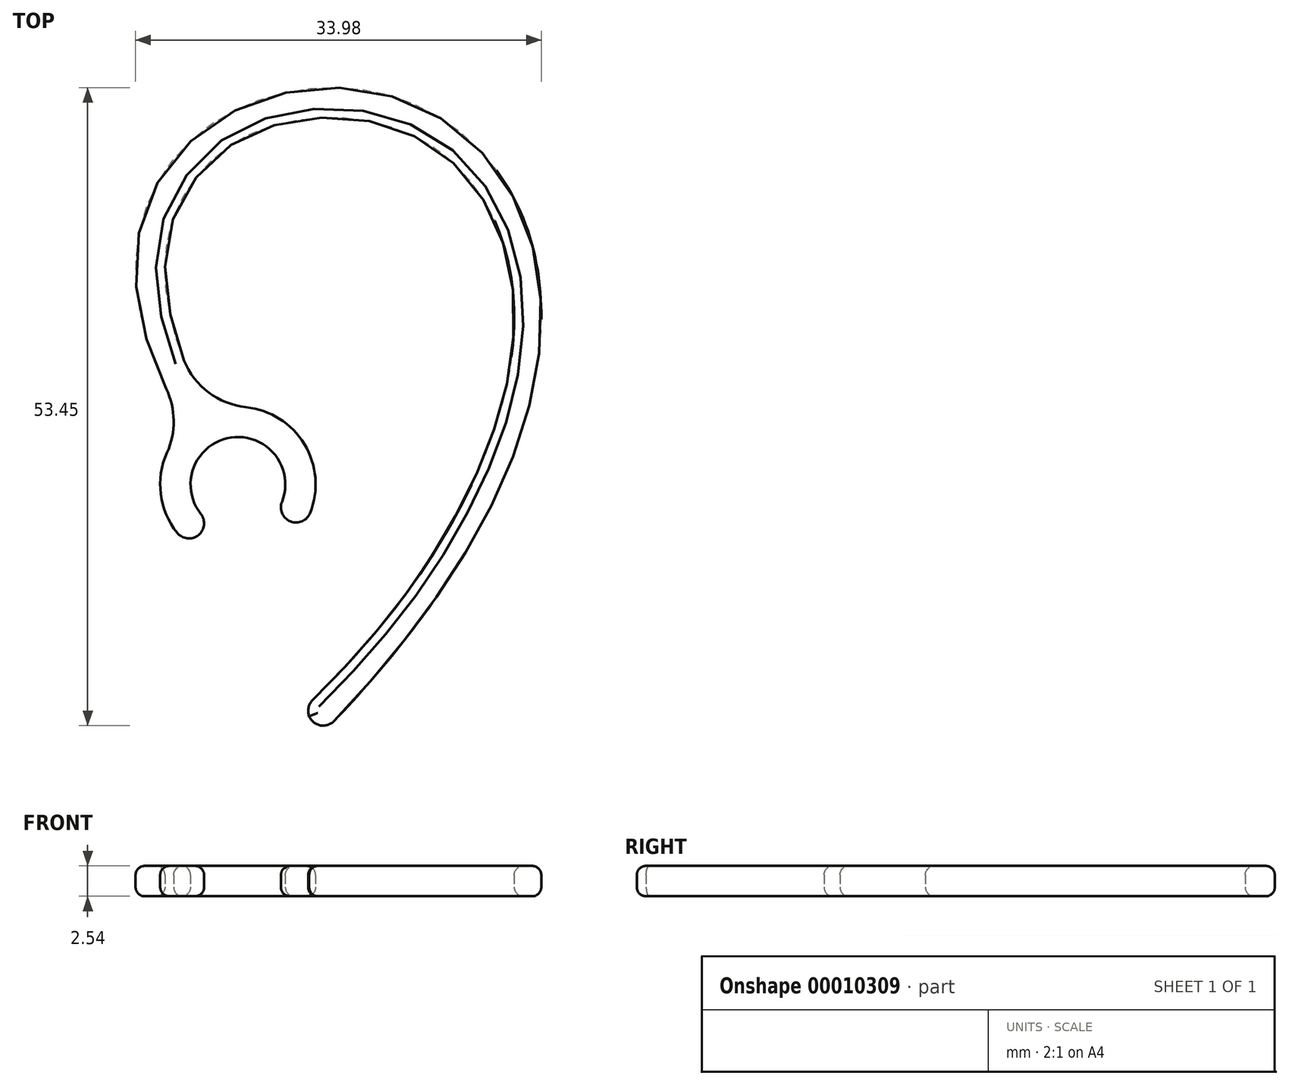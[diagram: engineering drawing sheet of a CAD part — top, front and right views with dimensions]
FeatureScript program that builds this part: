
annotation { "Feature Type Name" : "Feature", "Feature Type Description" : "" }
export const myFeature = defineFeature(function(context is Context, id is Id, definition is map)
    precondition{}
    {
        {
            var Q0;
            Q0=qCreatedBy(makeId("Top.planeOp"),FACE);
            var sketch = newSketch(context, id + "F0", { "sketchPlane" : qUnion([Q0])});
            skArc(sketch, "E0", {"start": v(3.23, -2.3) * mm, "mid": v(-0.58, 3.93) * mm, "end": v(-2.42, -3.15) * mm});
            skArc(sketch, "E1.0", {"start": v(5.3, -3.78) * mm, "mid": v(-0.96, 6.44) * mm, "end": v(-3.97, -5.16) * mm});
            skLineSegment(sketch, "E2", {"start": v(-2.42, -3.15) * mm, "end": v(-3.97, -5.16) * mm});
            skLineSegment(sketch, "E3", {"start": v(3.23, -2.3) * mm, "end": v(5.3, -3.78) * mm});
            skSolve(sketch);
        }
        {
            var Q0;
            Q0 = qSketchRegion(id + "F0", true);
            extrude(context, id + "F1", {"entities" : qUnion([Q0]), "depth" : 2.54 * mm});
        }
        {
            var Q0;
            Q0=qCreatedBy(makeId("Top.planeOp"),FACE);
            var sketch = newSketch(context, id + "F2", { "sketchPlane" : qUnion([Q0])});
            skFitSpline(sketch, "E4", {"points": [v(-2.9, 2.7) * mm, v(9.7, 33.15) * mm, v(6.7, -21.22) * mm], "startDerivative": vector(-95, 139.03) * mm, "endDerivative": vector(-160.2, -162.17) * mm});
            skFitSpline(sketch, "E5.0", {"points": [v(-0.8, 4.14) * mm, v(-2.68, 6.88) * mm, v(-4.63, 10.68) * mm, v(-5.82, 15.02) * mm, v(-6.11, 17.91) * mm, v(-5.9, 20.46) * mm, v(-5.25, 22.7) * mm, v(-4.23, 24.65) * mm, v(-2.43, 26.92) * mm, v(0.56, 29.13) * mm, v(4.2, 30.38) * mm, v(7.22, 30.74) * mm, v(9.46, 30.68) * mm, v(11.62, 30.3) * mm, v(14.38, 29.35) * mm, v(17.5, 27.42) * mm, v(20.48, 23.96) * mm, v(22.46, 19.4) * mm, v(23.14, 13.7) * mm, v(22.15, 6.89) * mm, v(19.11, -0.97) * mm, v(13.64, -9.75) * mm, v(8.15, -16.14) * mm, v(4.88, -19.44) * mm]});
            skLineSegment(sketch, "E6", {"start": v(5.66, -18.65) * mm, "end": v(6.7, -21.22) * mm});
            skArc(sketch, "E7.0", {"start": v(-0.97, 4.37) * mm, "mid": v(-2.17, 3.92) * mm, "end": v(-3.2, 3.14) * mm});
            skSolve(sketch);
        }
        {
            var Q0;
            Q0 = qSketchRegion(id + "F2", true);
            extrude(context, id + "F3", {"entities" : qUnion([Q0]), "operationType" : NewBodyOperationType.ADD, "depth" : 2.54 * mm});
        }
        {
            var Q0;
            Q0=makeQuery(id+"F3.boolean.opBoolean","INTERSECT",EDGE,{"derivedFrom":[makeQuery(id+"F1.opExtrude","SWEPT_FACE",FACE,{"disambiguationData":[OSD([sQuery(id+"F0.wireOp",EDGE,"E1.0")])]}),makeQuery(id+"F3.opExtrude","SWEPT_FACE",FACE,{"disambiguationData":[OSD([sQuery(id+"F2.wireOp",EDGE,"E4")])]})]});
            var Q1;
            Q1=makeQuery(id+"F3.boolean.opBoolean","INTERSECT",EDGE,{"derivedFrom":[makeQuery(id+"F1.opExtrude","SWEPT_FACE",FACE,{"disambiguationData":[OSD([sQuery(id+"F0.wireOp",EDGE,"E1.0")])]}),makeQuery(id+"F3.opExtrude","SWEPT_FACE",FACE,{"disambiguationData":[OSD([sQuery(id+"F2.wireOp",EDGE,"E5.0")])]})]});
            fillet(context, id + "F4", {"entities" : qUnion([Q0, Q1]), "radius" : 6.35 * mm, "tangentPropagation" : true, "allowEdgeOverflow" : false});
        }
        {
            var Q0;
            Q0=makeQuery(id+"F1.opExtrude","SWEPT_EDGE",EDGE,{"disambiguationData":[OSD([sQuery(id+"F0.wireOp",EDGE,"E0"),sQuery(id+"F0.wireOp",EDGE,"E3")])]});
            var Q1;
            Q1=makeQuery(id+"F1.opExtrude","SWEPT_EDGE",EDGE,{"disambiguationData":[OSD([sQuery(id+"F0.wireOp",EDGE,"E1.0"),sQuery(id+"F0.wireOp",EDGE,"E3")])]});
            var Q2;
            Q2=makeQuery(id+"F1.opExtrude","SWEPT_EDGE",EDGE,{"disambiguationData":[OSD([sQuery(id+"F0.wireOp",EDGE,"E1.0"),sQuery(id+"F0.wireOp",EDGE,"E2")])]});
            var Q3;
            Q3=makeQuery(id+"F1.opExtrude","SWEPT_EDGE",EDGE,{"disambiguationData":[OSD([sQuery(id+"F0.wireOp",EDGE,"E0"),sQuery(id+"F0.wireOp",EDGE,"E2")])]});
            var Q4;
            Q4=makeQuery(id+"F3.opExtrude","SWEPT_EDGE",EDGE,{"disambiguationData":[OSD([sQuery(id+"F2.wireOp",EDGE,"E4"),sQuery(id+"F2.wireOp",EDGE,"E6")])]});
            var Q5;
            Q5=makeQuery(id+"F3.opExtrude","SWEPT_EDGE",EDGE,{"disambiguationData":[OSD([sQuery(id+"F2.wireOp",EDGE,"E5.0"),sQuery(id+"F2.wireOp",EDGE,"E6")])]});
            fillet(context, id + "F5", {"entities" : qUnion([Q0, Q1, Q2, Q3, Q4, Q5]), "radius" : 1.27 * mm, "tangentPropagation" : true, "allowEdgeOverflow" : false});
        }
        {
            var Q0;
            Q0=makeQuery(id+"F3.boolean.opBoolean","MERGE",FACE,{"derivedFrom":[makeQuery(id+"F1.opExtrude","CAP_FACE",FACE,{"disambiguationData":[OSD([sQuery(id+"F0.wireOp",EDGE,"E0"),sQuery(id+"F0.wireOp",EDGE,"E1.0"),sQuery(id+"F0.wireOp",EDGE,"E2"),sQuery(id+"F0.wireOp",EDGE,"E3")])],"isStart":false}),makeQuery(id+"F3.opExtrude","CAP_FACE",FACE,{"disambiguationData":[OSD([sQuery(id+"F2.wireOp",EDGE,"E4"),sQuery(id+"F2.wireOp",EDGE,"E5.0"),sQuery(id+"F2.wireOp",EDGE,"E6"),sQuery(id+"F2.wireOp",EDGE,"E7.0")])],"isStart":false})]});
            var Q1;
            Q1=makeQuery(id+"F3.boolean.opBoolean","MERGE",FACE,{"derivedFrom":[makeQuery(id+"F1.opExtrude","CAP_FACE",FACE,{"disambiguationData":[OSD([sQuery(id+"F0.wireOp",EDGE,"E0"),sQuery(id+"F0.wireOp",EDGE,"E1.0"),sQuery(id+"F0.wireOp",EDGE,"E2"),sQuery(id+"F0.wireOp",EDGE,"E3")])],"isStart":true}),makeQuery(id+"F3.opExtrude","CAP_FACE",FACE,{"disambiguationData":[OSD([sQuery(id+"F2.wireOp",EDGE,"E4"),sQuery(id+"F2.wireOp",EDGE,"E5.0"),sQuery(id+"F2.wireOp",EDGE,"E6"),sQuery(id+"F2.wireOp",EDGE,"E7.0")])],"isStart":true})]});
            fillet(context, id + "F6", {"entities" : qUnion([Q0, Q1]), "radius" : 0.76 * mm, "tangentPropagation" : true, "allowEdgeOverflow" : false});
        }
    });
